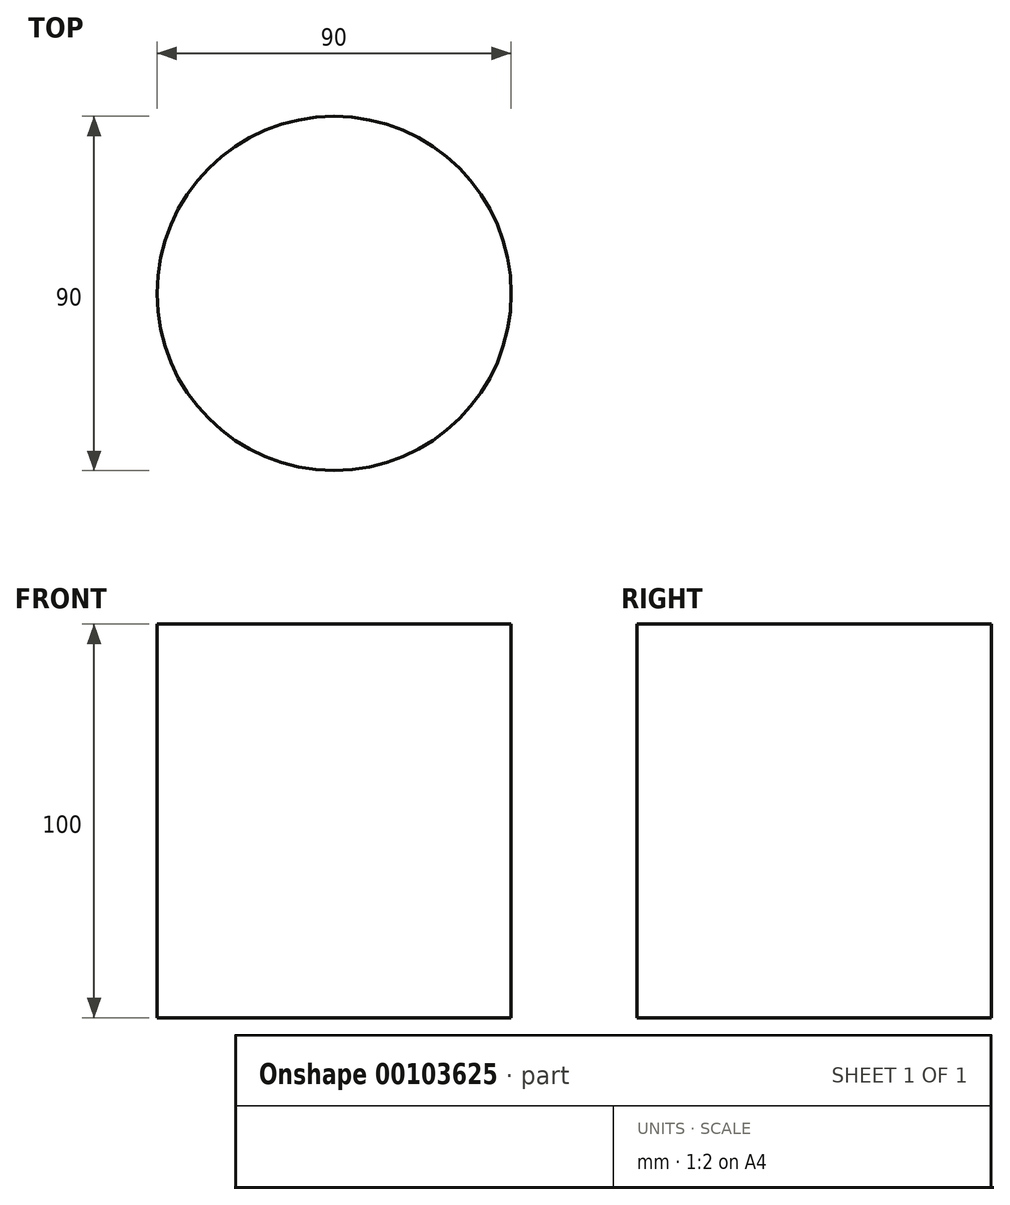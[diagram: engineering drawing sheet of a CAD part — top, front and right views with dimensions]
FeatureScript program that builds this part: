
annotation { "Feature Type Name" : "Feature", "Feature Type Description" : "" }
export const myFeature = defineFeature(function(context is Context, id is Id, definition is map)
    precondition{}
    {
        {
            var Q0;
            Q0=qCreatedBy(makeId("Top.planeOp"),FACE);
            var sketch = newSketch(context, id + "F0", { "sketchPlane" : qUnion([Q0])});
            skCircle(sketch, "E0", {"center": v(0, 0) * mm, "radius": 45 * mm});
            skSolve(sketch);
        }
        {
            var Q0;
            Q0=makeQuery(id+"F0.imprint","IMPRINT",FACE,{"disambiguationData":[TD([[makeQuery(id+"F0.imprint","IMPRINT",EDGE,{"derivedFrom":sQuery(id+"F0.wireOp",EDGE,"E0")}),1.0]])]});
            extrude(context, id + "F1", {"entities" : qUnion([Q0]), "depth" : 100 * mm});
        }
    });
